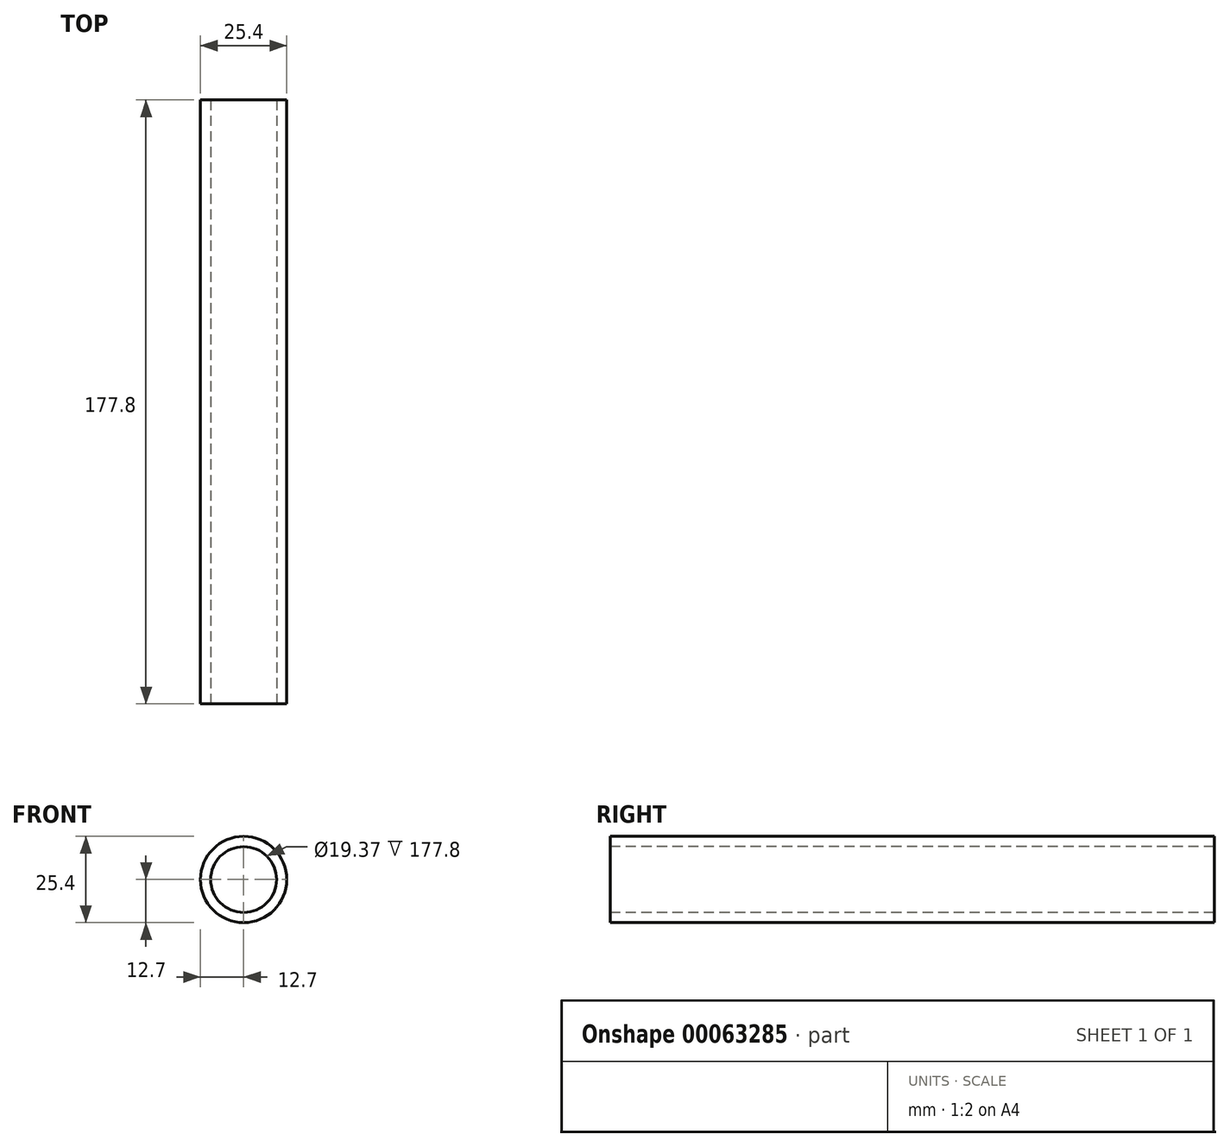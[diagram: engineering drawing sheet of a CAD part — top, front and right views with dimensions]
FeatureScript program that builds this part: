
annotation { "Feature Type Name" : "Feature", "Feature Type Description" : "" }
export const myFeature = defineFeature(function(context is Context, id is Id, definition is map)
    precondition{}
    {
        {
            var Q0;
            Q0=qCreatedBy(makeId("Front.planeOp"),FACE);
            var sketch = newSketch(context, id + "F0", { "sketchPlane" : qUnion([Q0])});
            skCircle(sketch, "E0", {"center": v(0, 0) * mm, "radius": 12.7 * mm});
            skSolve(sketch);
        }
        {
            var Q0;
            Q0 = qSketchRegion(id + "F0", true);
            extrude(context, id + "F1", {"entities" : qUnion([Q0]), "depth" : 177.8 * mm});
        }
        {
            var Q0;
            Q0=makeQuery(id+"F1.opExtrude","CAP_FACE",FACE,{"disambiguationData":[OSD([sQuery(id+"F0.wireOp",EDGE,"E0")])],"isStart":false});
            var sketch = newSketch(context, id + "F2", { "sketchPlane" : qUnion([Q0])});
            skCircle(sketch, "E1", {"center": v(0, 0) * mm, "radius": 9.69 * mm});
            skSolve(sketch);
        }
        {
            var Q0;
            Q0 = qSketchRegion(id + "F2", true);
            extrude(context, id + "F3", {"entities" : qUnion([Q0]), "operationType" : NewBodyOperationType.REMOVE, "oppositeDirection" : true, "depth" : 490.52 * mm});
        }
    });
